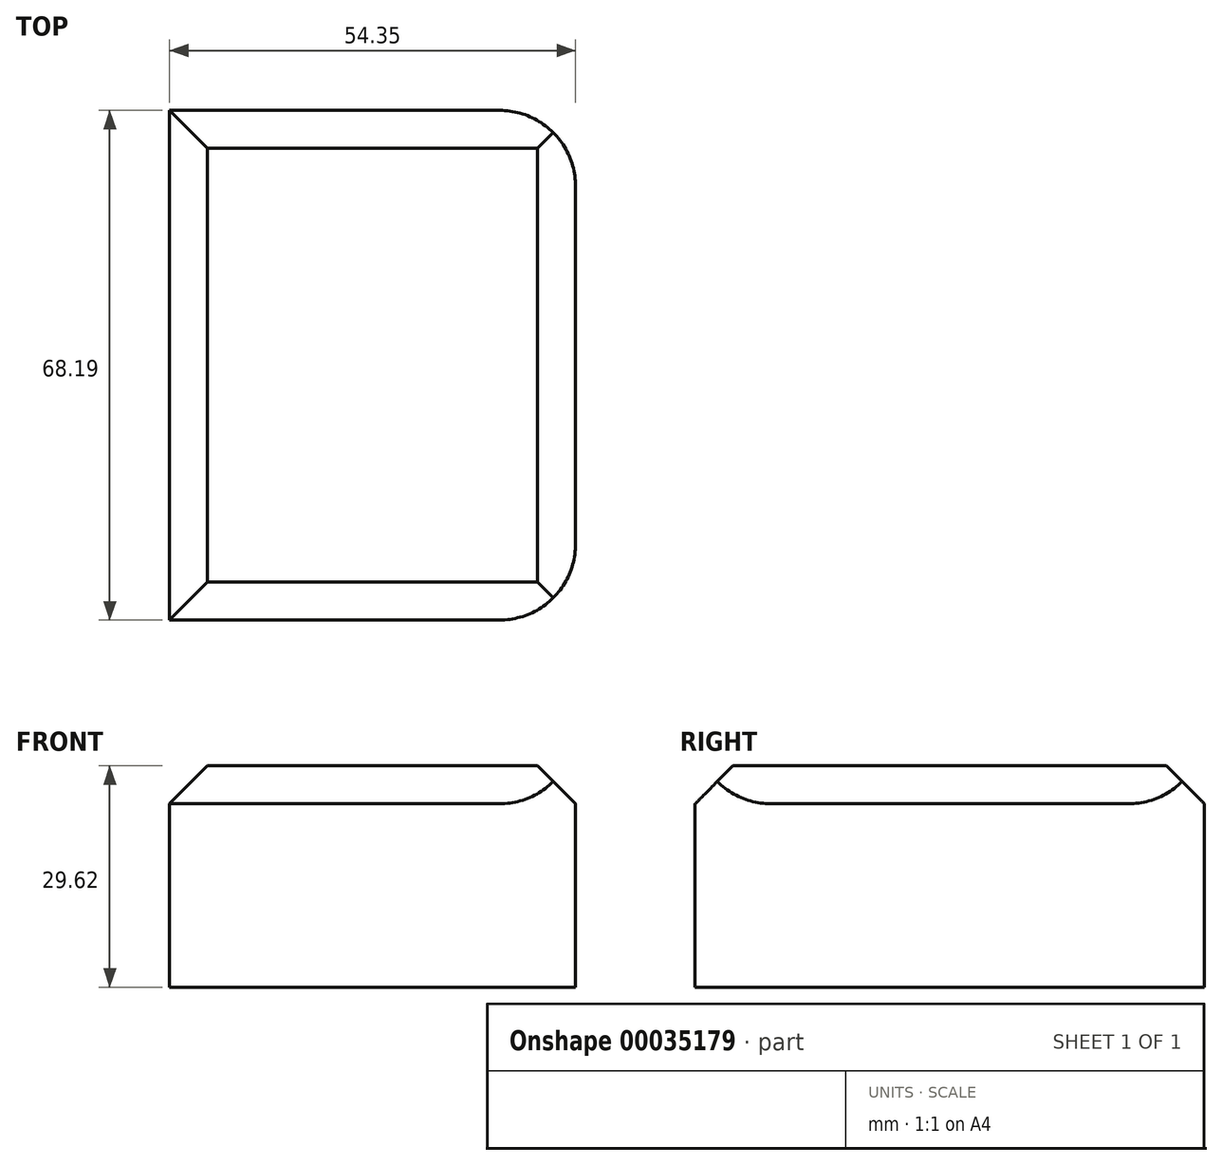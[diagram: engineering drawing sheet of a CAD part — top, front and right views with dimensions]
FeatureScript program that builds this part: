
annotation { "Feature Type Name" : "Feature", "Feature Type Description" : "" }
export const myFeature = defineFeature(function(context is Context, id is Id, definition is map)
    precondition{}
    {
        {
            var Q0;
            Q0=qCreatedBy(makeId("Front.planeOp"),FACE);
            var sketch = newSketch(context, id + "F0", { "sketchPlane" : qUnion([Q0])});
            skLineSegment(sketch, "E0.bottom", {"start": v(0, 0) * mm, "end": v(54.35, 0) * mm});
            skLineSegment(sketch, "E0.top", {"start": v(0, 29.62) * mm, "end": v(54.35, 29.62) * mm});
            skLineSegment(sketch, "E0.left", {"start": v(0, 0) * mm, "end": v(0, 29.62) * mm});
            skLineSegment(sketch, "E0.right", {"start": v(54.35, 0) * mm, "end": v(54.35, 29.62) * mm});
            skLineSegment(sketch, "E1.top", {"start": v(15.24, 12.94) * mm, "end": v(54.35, 12.94) * mm});
            skLineSegment(sketch, "E1.left", {"start": v(15.24, 29.62) * mm, "end": v(15.24, 12.94) * mm});
            skSolve(sketch);
        }
        {
            var Q0;
            {var subQ1=sQuery(id+"F0.wireOp",EDGE,"E1.top");Q0=makeQuery(id+"F0.imprint","IMPRINT",FACE,{"disambiguationData":[TD([[makeQuery(id+"F0.imprint","IMPRINT",EDGE,{"derivedFrom":subQ1}),1.0]])]});}
            var Q1;
            {var subQ2=sQuery(id+"F0.wireOp",EDGE,"E0.bottom");Q1=makeQuery(id+"F0.imprint","IMPRINT",FACE,{"disambiguationData":[TD([[makeQuery(id+"F0.imprint","IMPRINT",EDGE,{"derivedFrom":subQ2}),1.0]])]});}
            extrude(context, id + "F1", {"entities" : qUnion([Q0, Q1]), "depth" : 68.19 * mm});
        }
        {
            var Q0;
            Q0=makeQuery(id+"F1.opExtrude","SWEPT_EDGE",EDGE,{"disambiguationData":[OSD([sQuery(id+"F0.wireOp",EDGE,"E0.top"),sQuery(id+"F0.wireOp",EDGE,"E0.right")])]});
            var Q1;
            Q1=makeQuery(id+"F1.opExtrude","CAP_EDGE",EDGE,{"disambiguationData":[OSD([sQuery(id+"F0.wireOp",EDGE,"E0.top")])],"isStart":true});
            var Q2;
            Q2=makeQuery(id+"F1.opExtrude","SWEPT_EDGE",EDGE,{"disambiguationData":[OSD([sQuery(id+"F0.wireOp",EDGE,"E0.top"),sQuery(id+"F0.wireOp",EDGE,"E0.left")])]});
            var Q3;
            Q3=makeQuery(id+"F1.opExtrude","CAP_EDGE",EDGE,{"disambiguationData":[OSD([sQuery(id+"F0.wireOp",EDGE,"E0.top")])],"isStart":false});
            chamfer(context, id + "F2", {"entities" : qUnion([Q0, Q1, Q2, Q3]), "chamferType" : ChamferType.TWO_OFFSETS, "width1" : 5.08 * mm, "oppositeDirection" : false, "width2" : 5.08 * mm, "tangentPropagation" : true});
        }
        {
            var Q0;
            Q0=makeQuery(id+"F1.opExtrude","CAP_EDGE",EDGE,{"disambiguationData":[OSD([sQuery(id+"F0.wireOp",EDGE,"E0.right")])],"isStart":true});
            var Q1;
            Q1=makeQuery(id+"F1.opExtrude","CAP_EDGE",EDGE,{"disambiguationData":[OSD([sQuery(id+"F0.wireOp",EDGE,"E0.right")])],"isStart":false});
            fillet(context, id + "F3", {"entities" : qUnion([Q0, Q1]), "radius" : 10.16 * mm, "tangentPropagation" : true, "allowEdgeOverflow" : false});
        }
    });
